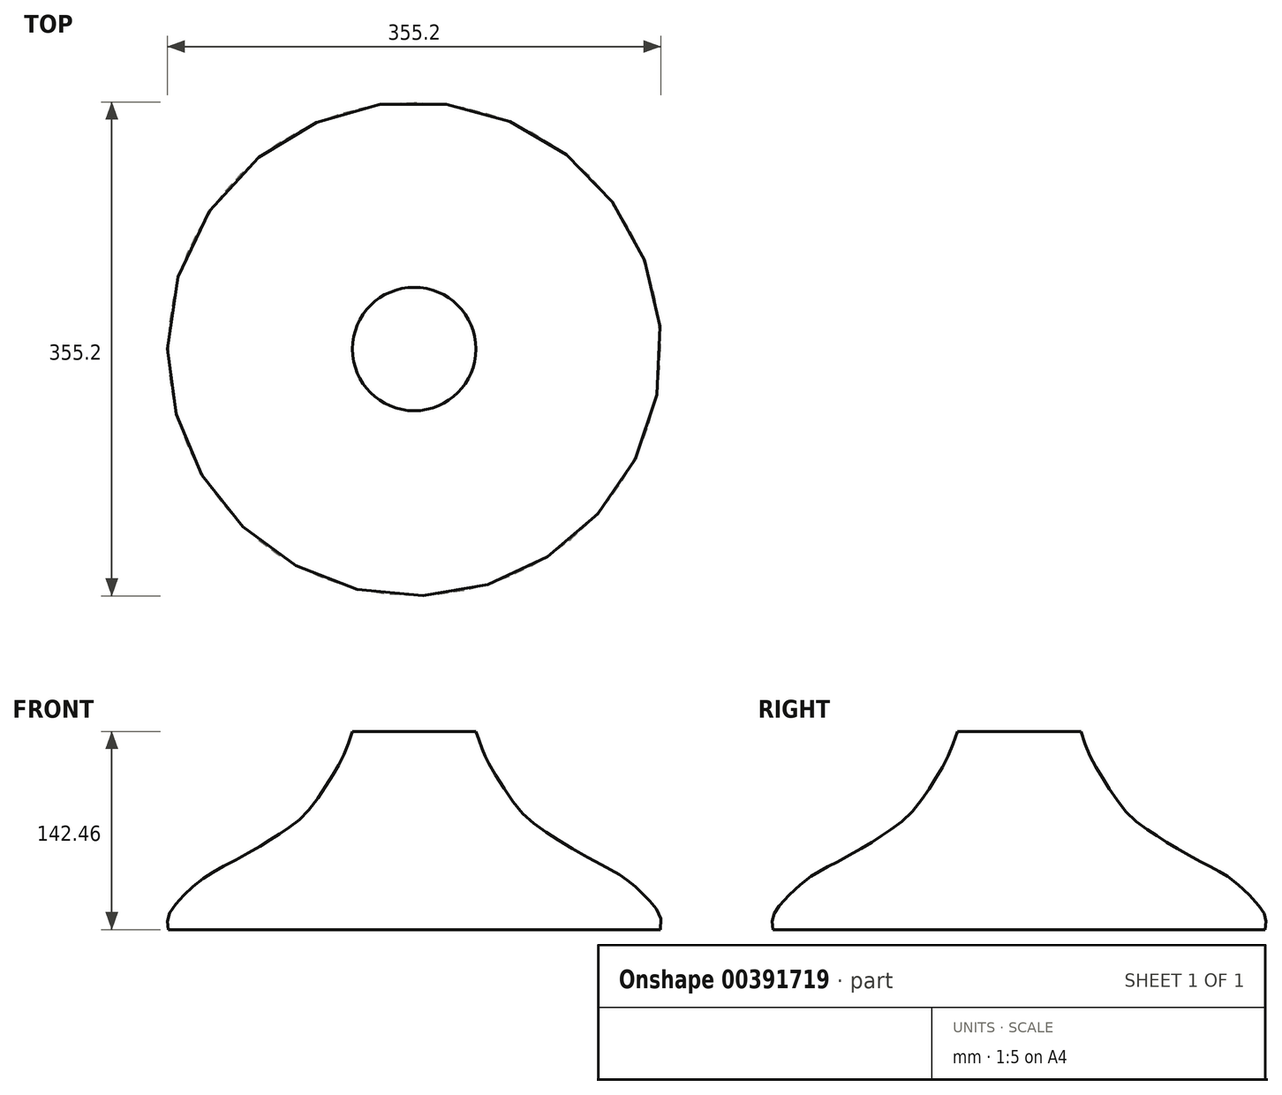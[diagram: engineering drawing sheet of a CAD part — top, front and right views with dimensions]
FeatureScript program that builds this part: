
annotation { "Feature Type Name" : "Feature", "Feature Type Description" : "" }
export const myFeature = defineFeature(function(context is Context, id is Id, definition is map)
    precondition{}
    {
        {
            var Q0;
            Q0=qCreatedBy(makeId("Front.planeOp"),FACE);
            var sketch = newSketch(context, id + "F0", { "sketchPlane" : qUnion([Q0])});
            skLineSegment(sketch, "E0", {"start": v(0, -76.25) * mm, "end": v(0, 66.2) * mm});
            skLineSegment(sketch, "E1", {"start": v(0, 66.2) * mm, "end": v(44.4, 66.2) * mm});
            skLineSegment(sketch, "E2", {"start": v(44.4, 66.2) * mm, "end": v(0, 66.2) * mm});
            skLineSegment(sketch, "E3", {"start": v(0, -76.25) * mm, "end": v(177.04, -76.25) * mm});
            skFitSpline(sketch, "E4", {"points": [v(44.4, 66.2) * mm, v(51.78, 46.97) * mm, v(61.6, 30.18) * mm, v(78.39, 6.85) * mm, v(95.17, -6.25) * mm, v(110.32, -16.07) * mm, v(134.06, -29.17) * mm, v(151.66, -39.4) * mm, v(168.04, -54.15) * mm, v(177.04, -66.84) * mm, v(177.04, -76.25) * mm], "startDerivative": vector(67.28, -197.01) * mm, "endDerivative": vector(-20.94, -135.77) * mm});
            skSolve(sketch);
        }
        {
            var Q0;
            Q0=makeQuery(id+"F0.imprint","IMPRINT",FACE,{"disambiguationData":[TD([[makeQuery(id+"F0.imprint","IMPRINT",EDGE,{"derivedFrom":sQuery(id+"F0.wireOp",EDGE,"E0")}),-1.0]])]});
            var Q1;
            Q1=sQuery(id+"F0.wireOp",EDGE,"E0");
            revolve(context, id + "F1", {"entities" : qUnion([Q0]), "axis" : qUnion([Q1]), "revolveType" : RevolveType.FULL});
        }
    });
